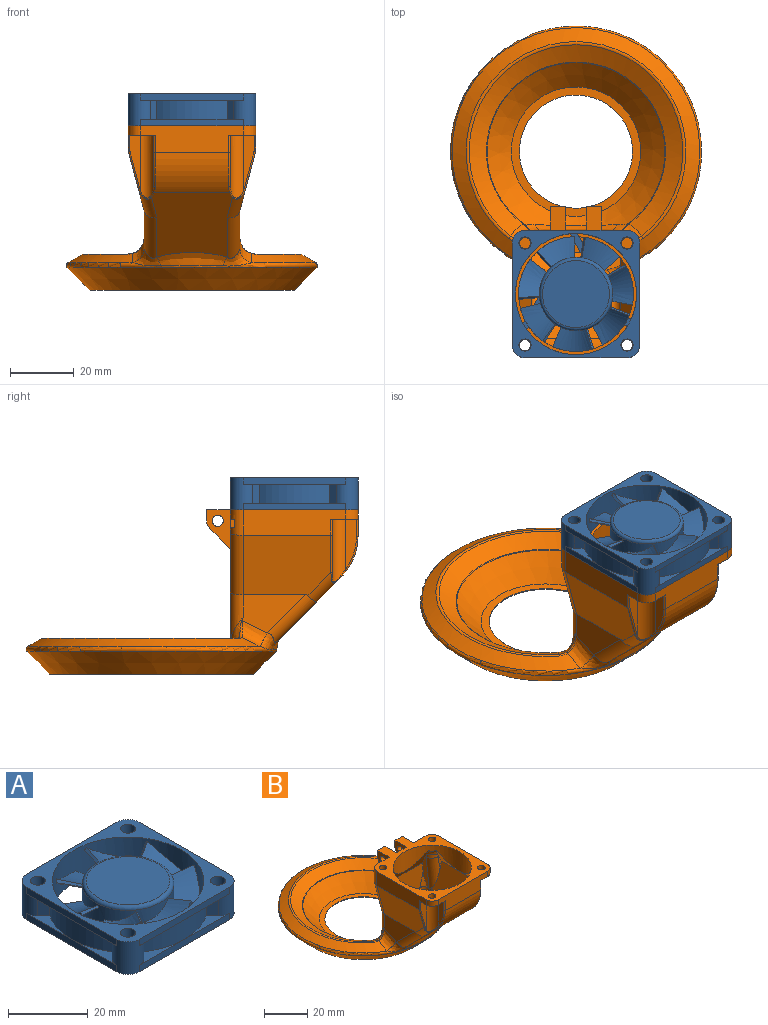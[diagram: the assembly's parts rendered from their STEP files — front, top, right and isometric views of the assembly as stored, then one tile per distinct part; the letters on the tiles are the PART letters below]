
ASSEMBLY  parts=2 mates=1
PART A: 102 faces, bbox 40x40x10.1 mm
  f0: plane 10.8x5.65mm, normal (0,0,1), area 19mm2, adj f2,f7,f8,f23
  f1: plane 11.32x2mm, normal (0,0,1), area 19mm2, adj f5,f6,f7,f23
  f2: plane 8.89x5.14mm, normal (-0.87,0.5,0), area 20.5mm2, adj f0,f7,f22,f23
  f3: plane 7.69x4.44mm, normal (-0.87,-0.5,0), area 17.8mm2, adj f7,f22,f23,f52
  f4: plane 8.89x5.14mm, normal (0.87,0.5,0), area 20.5mm2, adj f7,f22,f23,f52
  f5: plane 8.88x2mm, normal (0,1,0), area 17.8mm2, adj f1,f7,f22,f23
  f6: plane 10.27x2mm, normal (0,-1,0), area 20.5mm2, adj f1,f7,f22,f23
  f7: cylinder r=11.5mm len=23mm, axis (0,0,-1), area 590.9mm2, adj f0,f1,f2,f3,f4,f5,f6,f8
  f8: plane 7.69x4.44mm, normal (0.87,-0.5,0), area 17.8mm2, adj f0,f7,f22,f23
  f9: plane 32x2mm, normal (1,0,0), area 64mm2, adj f15,f17,f21,f26,f51
  f10: plane 32x2mm, normal (0,1,0), area 64mm2, adj f17,f19,f21,f44,f48
  f11: plane 32x2mm, normal (-1,0,0), area 64mm2, adj f13,f19,f22,f37,f41
  f12: plane 32x2mm, normal (0,-1,0), area 64mm2, adj f13,f15,f21,f30,f34
  f13: cylinder r=4mm len=10mm, axis (0,0,-1), area 100.5mm2, adj f11,f12,f14,f20,f21,f22,f32,f33
  f14: plane 32x2mm, normal (0,-1,0), area 64mm2, adj f13,f15,f22,f31,f33
  f15: cylinder r=4mm len=10mm, axis (0,0,-1), area 100.5mm2, adj f9,f12,f14,f16,f21,f22,f25,f26
  f16: plane 32x2mm, normal (1,0,0), area 64mm2, adj f15,f17,f22,f27,f50
  f17: cylinder r=4mm len=10mm, axis (0,0,-1), area 100.5mm2, adj f9,f10,f16,f18,f21,f22,f43,f44
  f18: plane 32x2mm, normal (0,1,0), area 64mm2, adj f17,f19,f22,f45,f47
  f19: cylinder r=4mm len=10mm, axis (0,0,-1), area 100.5mm2, adj f10,f11,f18,f20,f21,f22,f36,f37
  f20: plane 32x2mm, normal (-1,0,0), area 64mm2, adj f13,f19,f21,f38,f40
  f21: plane 40x40mm, normal (0,0,1), area 406.5mm2, adj f9,f10,f12,f13,f15,f17,f19,f20
  f22: plane 40x40mm, normal (0,0,-1), area 878.9mm2, adj f2,f3,f4,f5,f6,f7,f8,f11
  f23: cylinder r=19mm len=38mm, axis (0,0,-1), area 1180.2mm2, adj f0,f1,f2,f3,f4,f5,f6,f8
  f24: cylinder r=20mm len=22.06mm, axis (0,0,-1), area 140.2mm2, adj f25,f26,f27,f49,f50,f51
  f25: plane 6x2.14mm, normal (0.71,0.71,0), area 18.2mm2, adj f15,f24,f26,f27
  f26: plane 16x3.32mm, normal (0,0,-1), area 17.6mm2, adj f9,f15,f24,f25
  f27: plane 16x3.32mm, normal (0,0,1), area 17.6mm2, adj f15,f16,f24,f25
  f28: cylinder r=20mm len=22.06mm, axis (0,0,-1), area 140.2mm2, adj f29,f30,f31,f32,f33,f34
  f29: plane 6x2.14mm, normal (-0.71,-0.71,0), area 18.2mm2, adj f15,f28,f30,f31
  f30: plane 16x3.32mm, normal (0,0,-1), area 17.6mm2, adj f12,f15,f28,f29
  f31: plane 16x3.32mm, normal (0,0,1), area 17.6mm2, adj f14,f15,f28,f29
  f32: plane 6x2.14mm, normal (0.71,-0.71,0), area 18.2mm2, adj f13,f28,f33,f34
  f33: plane 16x3.32mm, normal (0,0,1), area 17.6mm2, adj f13,f14,f28,f32
  f34: plane 16x3.32mm, normal (0,0,-1), area 17.6mm2, adj f12,f13,f28,f32
  f35: cylinder r=20mm len=22.06mm, axis (0,0,1), area 140.2mm2, adj f36,f37,f38,f39,f40,f41
  f36: plane 6x2.14mm, normal (-0.71,-0.71,0), area 18.2mm2, adj f19,f35,f37,f38
  f37: plane 16x3.32mm, normal (0,0,1), area 17.6mm2, adj f11,f19,f35,f36
  f38: plane 16x3.32mm, normal (0,0,-1), area 17.6mm2, adj f19,f20,f35,f36
  f39: plane 6x2.14mm, normal (-0.71,0.71,0), area 18.2mm2, adj f13,f35,f40,f41
  f40: plane 16x3.32mm, normal (0,0,-1), area 17.6mm2, adj f13,f20,f35,f39
  f41: plane 16x3.32mm, normal (0,0,1), area 17.6mm2, adj f11,f13,f35,f39
  f42: cylinder r=20mm len=22.06mm, axis (0,0,-1), area 134.5mm2, adj f43,f44,f45,f46,f47,f48,f53,f54
  f43: plane 6x2.14mm, normal (-0.71,0.71,0), area 18.2mm2, adj f17,f42,f44,f45
  f44: plane 16x3.32mm, normal (0,0,-1), area 17.6mm2, adj f10,f17,f42,f43
  f45: plane 16x3.32mm, normal (0,0,1), area 17.6mm2, adj f17,f18,f42,f43
  f46: plane 6x2.14mm, normal (0.71,0.71,0), area 18.2mm2, adj f19,f42,f47,f48
  f47: plane 16x3.32mm, normal (0,0,1), area 17.6mm2, adj f18,f19,f42,f46
  f48: plane 16x3.32mm, normal (0,0,-1), area 17.6mm2, adj f10,f19,f42,f46
  f49: plane 6x2.14mm, normal (0.71,-0.71,0), area 18.2mm2, adj f17,f24,f50,f51
  f50: plane 16x3.32mm, normal (0,0,1), area 17.6mm2, adj f16,f17,f24,f49
  f51: plane 16x3.32mm, normal (0,0,-1), area 17.6mm2, adj f9,f17,f24,f49
  f52: plane 8.9x7.39mm, normal (0,0,1), area 19mm2, adj f3,f4,f7,f23
  f53: plane 2x0.49mm, normal (1,0,0), area 1mm2, adj f42,f54,f59,f60
  f54: plane 1.41x0.5mm, normal (0,0,-1), area 0.7mm2, adj f42,f53,f55,f60
  f55: plane 2x0.49mm, normal (-1,0,0), area 1mm2, adj f42,f54,f56,f60
  f56: plane 0.7x0.49mm, normal (0,0,-1), area 0.3mm2, adj f42,f55,f57,f60
  f57: plane 2x1.4mm, normal (-0.82,0,0.57), area 1.2mm2, adj f42,f56,f58,f60
  f58: plane 2x1.4mm, normal (0.82,0,0.57), area 1.2mm2, adj f42,f57,f59,f60
  f59: plane 0.7x0.49mm, normal (0,0,-1), area 0.3mm2, adj f42,f53,f58,f60
  f60: plane 4x2.8mm, normal (0,1,0), area 5.6mm2, adj f53,f54,f55,f56,f57,f58,f59
  f61: cylinder r=1.91mm len=10mm, axis (0,0,-1), area 119.7mm2, adj f21,f22
  f62: cylinder r=1.91mm len=10mm, axis (0,0,-1), area 119.7mm2, adj f21,f22
  f63: cylinder r=1.91mm len=10mm, axis (0,0,-1), area 119.7mm2, adj f21,f22
  f64: cylinder r=1.91mm len=10mm, axis (0,0,-1), area 119.7mm2, adj f21,f22
  f65: bspline ~19.33x13.36mm, area 78.9mm2, adj f7,f66,f68,f69
  f66: plane 5.1x4.8mm, normal (-0.46,-0.61,0.64), area 5.1mm2, adj f7,f65,f67,f69
  f67: bspline ~12.39x10.97mm, area 75.4mm2, adj f7,f66,f68,f69
  f68: plane 6.5x1.53mm, normal (1,0.02,-0.06), area 5mm2, adj f7,f65,f67,f69
  f69: cylinder r=18mm len=11.97mm, axis (0,0,-1), area 14.1mm2, adj f65,f66,f67,f68
  f70: torus R=10.5mm, axis (0,0,-1), area 109.9mm2, adj f7,f71
  f71: plane 21x21mm, normal (0,0,1), area 346.4mm2, adj f70
  f72: plane 5.79x3.05mm, normal (-0.89,-0.45,-0.06), area 5mm2, adj f7,f73,f75,f76
  f73: bspline ~18.05x17.14mm, area 78.9mm2, adj f7,f72,f74,f76
  f74: plane 6.24x2.83mm, normal (0.16,0.75,0.64), area 5.1mm2, adj f7,f73,f75,f76
  f75: bspline ~17.59x17.19mm, area 75.4mm2, adj f7,f72,f74,f76
  f76: cylinder r=18mm len=9.74mm, axis (0,0,-1), area 14.1mm2, adj f72,f73,f74,f75
  f77: plane 6.39x1.53mm, normal (-0.2,-0.98,-0.06), area 5mm2, adj f7,f78,f80,f81
  f78: bspline ~18.98x13.63mm, area 78.9mm2, adj f7,f77,f79,f81
  f79: plane 5.87x3.7mm, normal (-0.49,0.59,0.64), area 5.1mm2, adj f7,f78,f80,f81
  f80: bspline ~13.01x9.14mm, area 75.4mm2, adj f7,f77,f79,f81
  f81: cylinder r=18mm len=12.79mm, axis (0,0,-1), area 14.1mm2, adj f77,f78,f79,f80
  f82: plane 4.98x4.25mm, normal (0.64,-0.77,-0.06), area 5mm2, adj f7,f83,f85,f86
  f83: bspline ~19.08x14.71mm, area 78.9mm2, adj f7,f82,f84,f86
  f84: plane 6.5x1.87mm, normal (-0.76,-0.01,0.64), area 5.1mm2, adj f7,f83,f85,f86
  f85: bspline ~18.75x14.77mm, area 75.4mm2, adj f7,f82,f84,f86
  f86: cylinder r=18mm len=11.41mm, axis (0,0,-1), area 14.1mm2, adj f82,f83,f84,f85
  f87: plane 5.24x3.93mm, normal (0.6,0.79,-0.06), area 5mm2, adj f7,f88,f90,f91
  f88: bspline ~19.15x13.37mm, area 78.9mm2, adj f7,f87,f89,f91
  f89: plane 6.52x1.87mm, normal (0.18,-0.74,0.64), area 5.1mm2, adj f7,f88,f90,f91
  f90: bspline ~18.97x12.77mm, area 75.4mm2, adj f7,f87,f89,f91
  f91: cylinder r=18mm len=12.5mm, axis (0,0,-1), area 14.1mm2, adj f87,f88,f89,f90
  f92: plane 6.3x1.69mm, normal (-0.24,0.97,-0.06), area 5mm2, adj f7,f93,f95,f96
  f93: bspline ~13.18x12.45mm, area 78.9mm2, adj f7,f92,f94,f96
  f94: plane 5.66x4.06mm, normal (0.7,-0.32,0.64), area 5.1mm2, adj f7,f93,f95,f96
  f95: bspline ~12.66x12.25mm, area 75.4mm2, adj f7,f92,f94,f96
  f96: cylinder r=18mm len=10.55mm, axis (0,0,-1), area 14.1mm2, adj f92,f93,f94,f95
  f97: plane 5.96x2.68mm, normal (-0.91,0.41,-0.06), area 5mm2, adj f7,f98,f100,f101
  f98: bspline ~18.27x13.85mm, area 78.9mm2, adj f7,f97,f99,f101
  f99: plane 6.36x2.42mm, normal (0.68,0.35,0.64), area 5.1mm2, adj f7,f98,f100,f101
  f100: bspline ~13.22x7.73mm, area 75.4mm2, adj f7,f97,f99,f101
  f101: cylinder r=18mm len=12.97mm, axis (0,0,-1), area 14.1mm2, adj f97,f98,f99,f100
PART B: 180 faces, bbox 89.6x113.2x56 mm
  f0: cylinder r=26mm len=52mm, axis (0,0,-1), area 138.9mm2, adj f34,f176,f177,f179
  f1: cone r=39.29mm half-angle=45deg, axis (0,0,1), area 2109mm2, adj f85,f98,f99,f101,f105,f107,f176
  f2: cone r=20mm half-angle=45deg, axis (0,0,1), area 1486.2mm2, adj f65,f66,f68,f80,f81,f82,f173
  f3: cone r=20.71mm half-angle=45deg, axis (0,0,1), area 1395.9mm2, adj f84,f102,f103,f104,f106,f108,f172
  f4: plane 0.17x0.14mm, normal (0,0,-1), area 0mm2, adj f135,f137,f153
  f5: plane 0.17x0.14mm, normal (0,0,-1), area 0mm2, adj f135,f136,f154
  f6: plane 5.65x2.7mm, normal (-1,0,0), area 15.2mm2, adj f9,f18,f27,f152
  f7: plane 4.45x2.7mm, normal (1,0,0), area 12mm2, adj f9,f14,f18,f151
  f8: plane 0.17x0.14mm, normal (0,0,-1), area 0mm2, adj f135,f137,f154
  f9: plane 7.29x5.7mm, normal (0,0,1), area 26.2mm2, adj f6,f7,f14,f27,f148,f151,f152
  f10: plane 5.65x2.7mm, normal (1,0,0), area 15.2mm2, adj f19,f27,f144,f150
  f11: plane 4.45x2.7mm, normal (-1,0,0), area 12mm2, adj f13,f19,f144,f149
  f12: plane 0.17x0.14mm, normal (0,0,-1), area 0mm2, adj f135,f138,f153
  f13: cylinder r=4mm len=8mm, axis (0,0,1), area 40mm2, adj f11,f19,f27,f45,f56,f120,f144
  f14: cylinder r=4mm len=8mm, axis (0,0,-1), area 40mm2, adj f7,f9,f18,f27,f37,f58,f120
  f15: cylinder r=4mm len=4mm, axis (0,0,1), area 10.6mm2, adj f113,f115,f116,f137,f138,f153
  f16: cylinder r=1.75mm len=3.5mm, axis (0,0,1), area 33mm2, adj f18,f120
  f17: plane 0.17x0.14mm, normal (0,0,-1), area 0mm2, adj f22,f135,f136
  f18: plane 7.29x5.7mm, normal (0,0,-1), area 26.2mm2, adj f6,f7,f14,f16,f27,f151,f152
  f19: plane 7.29x5.7mm, normal (0,0,-1), area 26.2mm2, adj f10,f11,f13,f27,f143,f149,f150
  f20: cylinder r=17mm len=22.58mm, axis (-1,0,0), area 107.2mm2, adj f86,f135
  f21: cylinder r=5mm len=19.89mm, axis (0,0,1), area 101.9mm2, adj f23,f28,f86,f89,f92,f135,f138,f141
  f22: cylinder r=5mm len=19.88mm, axis (0,0,1), area 101.9mm2, adj f17,f31,f86,f90,f94,f135,f136,f142
  f23: plane 0.17x0.14mm, normal (0,0,-1), area 0mm2, adj f21,f135,f138
  f24: plane 6.48x6.48mm, normal (0,0.71,-0.71), area 43.5mm2, adj f26,f27,f130,f131
  f25: plane 4.75x3.5mm, normal (0,1,0), area 16.6mm2, adj f26,f120,f130,f131
  f26: cylinder r=3.5mm len=4.75mm, axis (-1,0,0), area 13.1mm2, adj f24,f25,f130,f131
  f27: plane 44.76x32mm, normal (0,1,0), area 997.5mm2, adj f6,f9,f10,f13,f14,f18,f19,f24
  f28: plane 31.36x19.86mm, normal (-0.97,0,0.26), area 351.9mm2, adj f21,f87,f89,f91,f92,f115,f116,f138
  f29: plane 31.76x26.23mm, normal (0,-1,0), area 713mm2, adj f30,f95,f96,f97,f104,f110,f114,f137
  f30: cylinder r=3mm len=8.66mm, axis (0.26,0,0.97), area 19.2mm2, adj f29,f95,f114
  f31: plane 31.36x19.86mm, normal (0.97,0,0.26), area 351.9mm2, adj f22,f88,f90,f93,f94,f112,f118,f136
  f32: cone r=28mm half-angle=60deg, axis (0,0,1), area 953.2mm2, adj f64,f70,f75,f81
  f33: torus R=38.37mm, axis (0,0,-1), area 413mm2, adj f35,f36,f60,f61,f63,f67,f69
  f34: plane 64x64mm, normal (0,0,-1), area 1127.8mm2, adj f0,f35,f177,f178,f179
  f35: cone r=40mm half-angle=45deg, axis (0,0,1), area 2235.3mm2, adj f33,f34
  f36: cone r=34mm half-angle=60deg, axis (0,0,-1), area 966.2mm2, adj f33,f62,f71,f74,f75,f76
  f37: plane 32x8mm, normal (-1,0,0), area 233.5mm2, adj f14,f39,f119,f120,f122,f156
  f38: plane 32x8.37mm, normal (0,-1,0), area 219.5mm2, adj f42,f119,f120,f121,f122,f123,f155,f163
  f39: plane 27.68x19.09mm, normal (-0.97,0,-0.26), area 506.3mm2, adj f37,f44,f54,f55,f58,f158
  f40: plane 25.44x20.13mm, normal (0,-0.71,-0.71), area 616mm2, adj f42,f52,f53,f54,f55,f63,f161,f166
  f41: plane 27.68x19.09mm, normal (0.97,0,-0.26), area 506.3mm2, adj f43,f45,f52,f53,f56,f169
  f42: cylinder r=18mm len=23.61mm, axis (-1,0,0), area 325.9mm2, adj f38,f40,f157,f159,f164,f165
  f43: plane 19.83x12mm, normal (1,0,0), area 148.2mm2, adj f41,f52,f57,f60,f62,f78
  f44: plane 19.91x12.08mm, normal (-1,0,0), area 148.2mm2, adj f39,f54,f59,f69,f71,f72
  f45: plane 32x8mm, normal (1,0,0), area 233.5mm2, adj f13,f41,f120,f121,f123,f167
  f46: plane 17.65x3.5mm, normal (0,-1,0), area 40.1mm2, adj f47,f123,f167,f169,f170
  f47: cylinder r=4mm len=19.72mm, axis (0,0,1), area 116.2mm2, adj f46,f48,f123,f165,f166,f168
  f48: plane 15.87x3.5mm, normal (1,0,0), area 43.8mm2, adj f47,f123,f163,f164
  f49: cylinder r=4mm len=19.72mm, axis (0,0,1), area 116.2mm2, adj f50,f51,f119,f159,f161,f162
  f50: plane 17.65x3.5mm, normal (0,-1,0), area 40.1mm2, adj f49,f119,f156,f158,f160
  f51: plane 15.87x3.5mm, normal (-1,0,0), area 43.8mm2, adj f49,f119,f155,f157
  f52: cylinder r=4mm len=15.66mm, axis (0,-0.71,0.71), area 109.6mm2, adj f40,f41,f43,f53,f61
  f53: cylinder r=4mm len=10.29mm, axis (-0.19,0.69,-0.69), area 49.5mm2, adj f40,f41,f52,f168,f170
  f54: cylinder r=4mm len=15.66mm, axis (0,0.71,-0.71), area 109.6mm2, adj f39,f40,f44,f55,f67
  f55: cylinder r=4mm len=10.29mm, axis (0.19,0.69,-0.69), area 49.5mm2, adj f39,f40,f54,f160,f162
  f56: cylinder r=4mm len=20.2mm, axis (0.26,0,0.97), area 121.4mm2, adj f13,f27,f41,f57
  f57: cylinder r=4mm len=15.77mm, axis (0,0,-1), area 70.8mm2, adj f27,f43,f56,f64,f65
  f58: cylinder r=4mm len=20.2mm, axis (0.26,0,-0.97), area 121.4mm2, adj f14,f27,f39,f59
  f59: cylinder r=4mm len=15.77mm, axis (0,0,1), area 70.8mm2, adj f27,f44,f58,f68,f70
  f60: bspline ~4.62x3.91mm, area 0.3mm2, adj f33,f43,f61,f62
  f61: bspline ~10.8x6.2mm, area 28.9mm2, adj f33,f52,f60,f63
  f62: bspline ~14.97x10.63mm, area 48.7mm2, adj f36,f43,f60,f77
  f63: bspline ~23.03x4.22mm, area 84.2mm2, adj f33,f40,f61,f67
  f64: bspline ~11.17x10.27mm, area 39.8mm2, adj f32,f57,f76,f77,f78,f82,f83
  f65: bspline ~6.77x6.37mm, area 15.8mm2, adj f2,f57,f66,f83
  f66: bspline ~33.16x8.27mm, area 102.5mm2, adj f2,f27,f65,f68
  f67: bspline ~10x5.76mm, area 28.9mm2, adj f33,f54,f63,f69
  f68: bspline ~6.77x6.37mm, area 15.8mm2, adj f2,f59,f66,f79
  f69: bspline ~4.62x3.91mm, area 0.3mm2, adj f33,f44,f67,f71
  f70: bspline ~11.27x9.95mm, area 39.8mm2, adj f32,f59,f72,f73,f74,f79,f80
  f71: bspline ~20.56x13.54mm, area 48.7mm2, adj f36,f44,f69,f73
  f72: bspline ~3.17x1.46mm, area 0.1mm2, adj f44,f70,f73
  f73: bspline ~5.59x4.69mm, area 5.6mm2, adj f70,f71,f72,f74
  f74: bspline ~4.76x2.7mm, area 2.6mm2, adj f36,f70,f73,f75
  f75: torus R=34mm, axis (0,0,-1), area 176.9mm2, adj f32,f36,f74,f76
  f76: bspline ~4.76x2.7mm, area 2.6mm2, adj f36,f64,f75,f77
  f77: bspline ~5.59x4.69mm, area 5.6mm2, adj f62,f64,f76,f78
  f78: bspline ~3.17x1.46mm, area 0.1mm2, adj f43,f64,f77
  f79: bspline ~3.96x3.53mm, area 0.6mm2, adj f68,f70,f80
  f80: bspline ~1.4x1.23mm, area 0.2mm2, adj f2,f70,f79,f81
  f81: torus R=28.61mm, axis (0,0,-1), area 36.9mm2, adj f2,f32,f80,f82
  f82: bspline ~1.4x1.23mm, area 0.2mm2, adj f2,f64,f81,f83
  f83: bspline ~4.24x4.09mm, area 0.6mm2, adj f64,f65,f82
  f84: cone r=28.5mm half-angle=60deg, axis (0,0,1), area 968.7mm2, adj f3,f85,f102,f108
  f85: cone r=33.5mm half-angle=60deg, axis (0,0,-1), area 953mm2, adj f1,f84,f100,f102,f108,f109
  f86: plane 25.4x20.25mm, normal (0,0.71,0.71), area 614.3mm2, adj f20,f21,f22,f91,f92,f93,f94,f101
  f87: plane 19.96x12.13mm, normal (-1,0,0), area 150.8mm2, adj f28,f91,f95,f98,f100,f102
  f88: plane 19.96x12.13mm, normal (1,0,0), area 150.8mm2, adj f31,f93,f97,f107,f108,f109
  f89: plane 12.06x2.1mm, normal (0,1,0), area 12.7mm2, adj f21,f28,f138
  f90: plane 12.06x2.1mm, normal (0,1,0), area 12.7mm2, adj f22,f31,f136
  f91: cylinder r=3mm len=14.95mm, axis (0,-0.71,0.71), area 82.5mm2, adj f28,f86,f87,f92,f99
  f92: cylinder r=3mm len=9.09mm, axis (-0.19,0.69,-0.69), area 38.7mm2, adj f21,f28,f86,f91
  f93: cylinder r=3mm len=14.95mm, axis (0,0.71,-0.71), area 82.5mm2, adj f31,f86,f88,f94,f105
  f94: cylinder r=3mm len=9.09mm, axis (0.19,0.69,-0.69), area 38.7mm2, adj f22,f31,f86,f93
  f95: cylinder r=3mm len=15.77mm, axis (0,0,-1), area 53.4mm2, adj f29,f30,f87,f102,f103
  f96: cylinder r=3mm len=8.66mm, axis (0.26,0,-0.97), area 19.2mm2, adj f29,f97,f110
  f97: cylinder r=3mm len=15.77mm, axis (0,0,1), area 53.4mm2, adj f29,f88,f96,f106,f108
  f98: bspline ~5.35x4.69mm, area 0.3mm2, adj f1,f87,f99,f100
  f99: bspline ~10.84x5.81mm, area 26.6mm2, adj f1,f91,f98,f101
  f100: bspline ~15.35x11.5mm, area 58.4mm2, adj f85,f87,f98,f102
  f101: bspline ~23.03x4.74mm, area 99.6mm2, adj f1,f86,f99,f105
  f102: bspline ~12.03x10.28mm, area 44.1mm2, adj f3,f84,f85,f87,f95,f100,f103
  f103: bspline ~7.48x6.75mm, area 18.1mm2, adj f3,f95,f102,f104
  f104: bspline ~34x8.98mm, area 124.7mm2, adj f3,f29,f103,f106
  f105: bspline ~10.01x5.46mm, area 26.6mm2, adj f1,f93,f101,f107
  f106: bspline ~7.48x6.75mm, area 18.1mm2, adj f3,f97,f104,f108
  f107: bspline ~5.35x4.69mm, area 0.3mm2, adj f1,f88,f105,f109
  f108: bspline ~12.14x10.03mm, area 44.1mm2, adj f3,f84,f85,f88,f97,f106,f109
  f109: bspline ~15.43x11.55mm, area 58.4mm2, adj f85,f88,f107,f108
  f110: plane 21.93x6.27mm, normal (0.99,0,-0.11), area 44.3mm2, adj f29,f96,f111,f118,f137
  f111: plane 0.87x0.43mm, normal (1,0,0), area 0.2mm2, adj f110,f117,f137
  f112: plane 8.8x2.1mm, normal (0,-1,0), area 7.7mm2, adj f31,f117,f118,f136
  f113: plane 0.87x0.43mm, normal (-1,0,0), area 0.2mm2, adj f15,f114,f137
  f114: plane 21.93x6.27mm, normal (-0.99,0,-0.11), area 44.3mm2, adj f29,f30,f113,f116,f137
  f115: plane 8.8x2.1mm, normal (0,-1,0), area 7.7mm2, adj f15,f28,f116,f138
  f116: cylinder r=4mm len=19.09mm, axis (-0.11,0,0.99), area 84.7mm2, adj f15,f28,f114,f115
  f117: cylinder r=4mm len=4mm, axis (0,0,-1), area 10.6mm2, adj f111,f112,f118,f136,f137,f154
  f118: cylinder r=4mm len=19.09mm, axis (-0.11,0,-0.99), area 84.7mm2, adj f31,f110,f112,f117
  f119: plane 8.5x8.5mm, normal (0,0,-1), area 47.6mm2, adj f37,f38,f49,f50,f51,f122,f125,f155
  f120: plane 47.5x40mm, normal (0,0,1), area 601.2mm2, adj f13,f14,f16,f25,f27,f37,f38,f45
  f121: cylinder r=4mm len=4mm, axis (0,0,-1), area 18.8mm2, adj f38,f45,f120,f123
  f122: cylinder r=4mm len=4mm, axis (0,0,-1), area 18.8mm2, adj f37,f38,f119,f120
  f123: plane 8.5x8.5mm, normal (0,0,-1), area 47.6mm2, adj f38,f45,f46,f47,f48,f121,f124,f163
  f124: cylinder r=1.75mm len=3.5mm, axis (0,0,1), area 33mm2, adj f120,f123
  f125: cylinder r=1.75mm len=3.5mm, axis (0,0,1), area 33mm2, adj f119,f120
  f126: plane 6.48x6.48mm, normal (0,0.71,-0.71), area 43.5mm2, adj f27,f127,f129,f132
  f127: cylinder r=3.5mm len=4.75mm, axis (-1,0,0), area 13.1mm2, adj f126,f128,f129,f132
  f128: plane 4.75x3.5mm, normal (0,1,0), area 16.6mm2, adj f120,f127,f129,f132
  f129: plane 12.45x7.5mm, normal (1,0,0), area 55.4mm2, adj f27,f120,f126,f127,f128,f133
  f130: plane 12.45x7.5mm, normal (-1,0,0), area 55.4mm2, adj f24,f25,f26,f27,f120,f134
  f131: plane 12.45x7.5mm, normal (1,0,0), area 55.4mm2, adj f24,f25,f26,f27,f120,f134
  f132: plane 12.45x7.5mm, normal (-1,0,0), area 55.4mm2, adj f27,f120,f126,f127,f128,f133
  f133: cylinder r=1.75mm len=4.75mm, axis (1,0,0), area 52.2mm2, adj f129,f132
  f134: cylinder r=1.75mm len=4.75mm, axis (1,0,0), area 52.2mm2, adj f130,f131
  f135: cylinder r=18mm len=36mm, axis (0,0,1), area 1065.4mm2, adj f4,f5,f8,f12,f17,f20,f21,f22
  f136: plane 23.55x8.3mm, normal (0.89,0,-0.45), area 73mm2, adj f5,f17,f22,f31,f90,f112,f117,f135
  f137: plane 25.1x10mm, normal (0,-0.89,-0.45), area 132.4mm2, adj f4,f8,f15,f29,f110,f111,f113,f114
  f138: plane 23.55x8.3mm, normal (-0.89,0,-0.45), area 73mm2, adj f12,f15,f21,f23,f28,f89,f115,f135
  f139: cone r=18mm half-angle=45deg, axis (0,0,1), area 0mm2, adj f135,f142
  f140: cone r=18mm half-angle=45deg, axis (0,0,1), area 0mm2, adj f135,f141
  f141: bspline ~3.06x2.91mm, area 2.7mm2, adj f21,f135,f140
  f142: bspline ~3.06x2.91mm, area 2.7mm2, adj f22,f135,f139
  f143: cylinder r=1.75mm len=3.5mm, axis (0,0,1), area 33mm2, adj f19,f120
  f144: plane 7.29x5.7mm, normal (0,0,1), area 26.2mm2, adj f10,f11,f13,f27,f146,f149,f150
  f145: plane 3.5x3.5mm, normal (0,0,1), area 9.6mm2, adj f146
  f146: cylinder r=1.75mm len=9.3mm, axis (0,0,1), area 102.3mm2, adj f144,f145
  f147: plane 3.5x3.5mm, normal (0,0,1), area 9.6mm2, adj f148
  f148: cylinder r=1.75mm len=9.3mm, axis (0,0,1), area 102.3mm2, adj f9,f147
  f149: plane 2.85x2.7mm, normal (-0.5,0.87,0), area 8.9mm2, adj f11,f19,f144,f150
  f150: plane 2.85x2.7mm, normal (0.5,0.87,0), area 8.9mm2, adj f10,f19,f144,f149
  f151: plane 2.85x2.7mm, normal (0.5,0.87,0), area 8.9mm2, adj f7,f9,f18,f152
  f152: plane 2.85x2.7mm, normal (-0.5,0.87,0), area 8.9mm2, adj f6,f9,f18,f151
  f153: bspline ~5.24x5.24mm, area 12.3mm2, adj f4,f12,f15,f135,f137,f138
  f154: bspline ~5.24x5.24mm, area 12.3mm2, adj f5,f8,f117,f135,f136,f137
  f155: cylinder r=0.5mm len=5.37mm, axis (0,0,1), area 4.2mm2, adj f38,f51,f119,f157
  f156: cylinder r=0.5mm len=5mm, axis (0,0,-1), area 3.9mm2, adj f37,f50,f119,f158
  f157: torus R=17.5mm, axis (1,0,0), area 9mm2, adj f42,f51,f155,f159
  f158: cylinder r=0.5mm len=11.83mm, axis (-0.26,0,0.97), area 9.5mm2, adj f39,f50,f156,f160
  f159: bspline ~4.17x3.4mm, area 1.8mm2, adj f42,f49,f157,f161
  f160: bspline ~1.28x0.86mm, area 0.9mm2, adj f50,f55,f158,f162
  f161: bspline ~1.81x1.48mm, area 1.3mm2, adj f40,f49,f159,f162
  f162: bspline ~4.41x3.2mm, area 2.4mm2, adj f49,f55,f160,f161
  f163: cylinder r=0.5mm len=5.37mm, axis (0,0,-1), area 4.2mm2, adj f38,f48,f123,f164
  f164: torus R=17.5mm, axis (1,0,0), area 9mm2, adj f42,f48,f163,f165
  f165: bspline ~4.17x3.4mm, area 1.8mm2, adj f42,f47,f164,f166
  f166: bspline ~1.81x1.48mm, area 1.3mm2, adj f40,f47,f165,f168
  f167: cylinder r=0.5mm len=5mm, axis (0,0,1), area 3.9mm2, adj f45,f46,f123,f169
  f168: bspline ~4.15x3.2mm, area 2.4mm2, adj f47,f53,f166,f170
  f169: cylinder r=0.5mm len=11.83mm, axis (-0.26,0,-0.97), area 9.5mm2, adj f41,f46,f167,f170
  f170: bspline ~2.51x1.28mm, area 0.9mm2, adj f46,f53,f168,f169
  f171: cylinder r=22.63mm len=45.27mm, axis (0,0,-1), area 42.7mm2, adj f172,f175
  f172: plane 45.27x45.27mm, normal (0,0,1), area 128.3mm2, adj f3,f171
  f173: plane 40.6x40.6mm, normal (0,0,1), area 304.8mm2, adj f2,f174
  f174: cylinder r=17.75mm len=35.5mm, axis (0,0,-1), area 33.5mm2, adj f173,f175
  f175: plane 45.27x45.27mm, normal (0,0,-1), area 619.8mm2, adj f171,f174
  f176: plane 63.17x63.17mm, normal (0,0,1), area 1045mm2, adj f0,f1,f177,f178,f179
  f177: plane 1.86x1mm, normal (-0.43,0.9,0), area 2.1mm2, adj f0,f34,f176,f178
  f178: cylinder r=23.5mm len=19.86mm, axis (0,0,-1), area 20.5mm2, adj f34,f176,f177,f179
  f179: plane 1.86x1mm, normal (0.43,0.9,0), area 2.1mm2, adj f0,f34,f176,f178
PLACE A t=(0,-24,3.5)mm
PLACE B at identity fixed
MATE fastened A.f17 <-> B.f13  axis (0,0,-1) through (16,-8,3.5)mm
